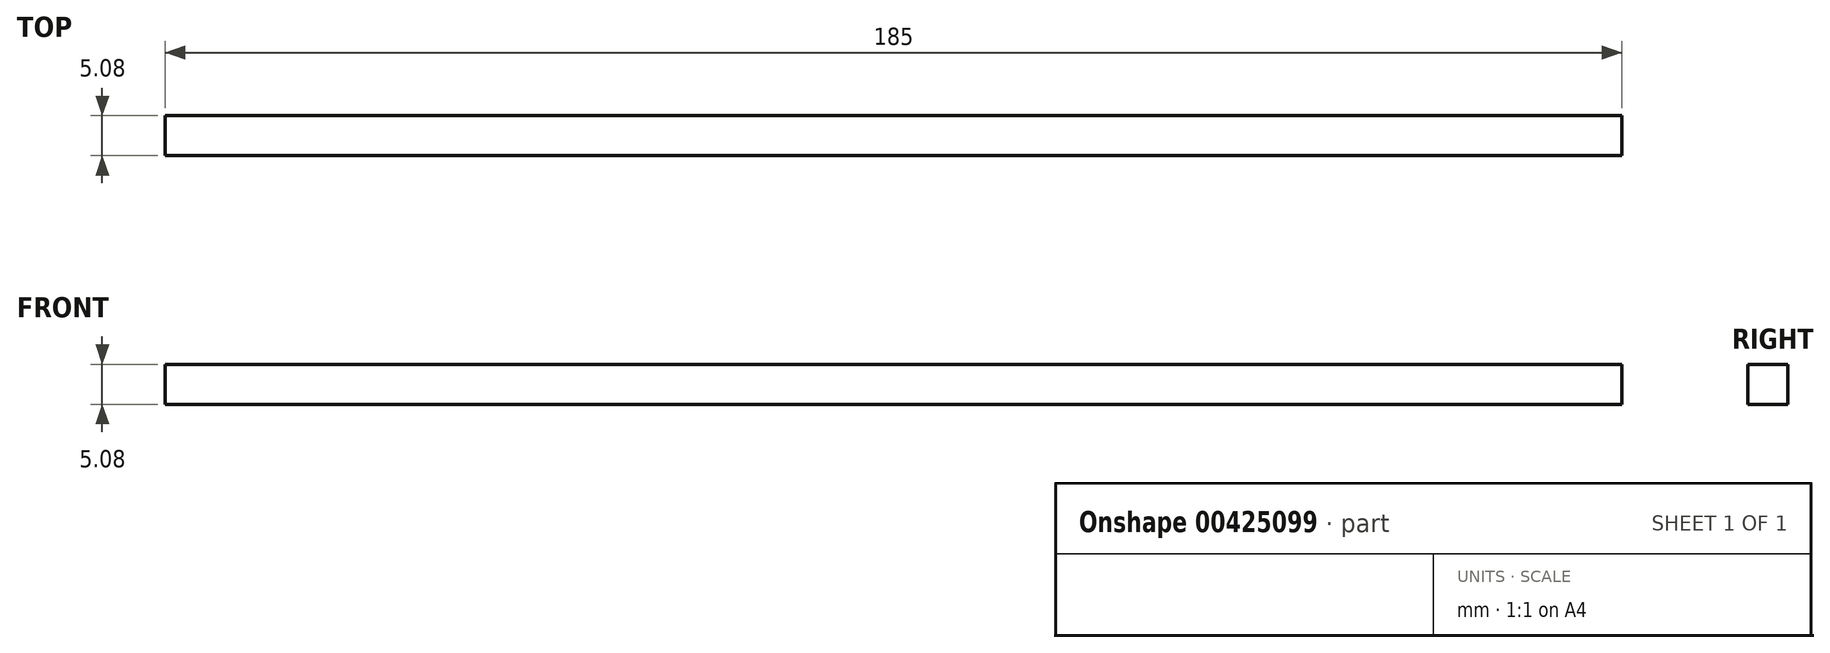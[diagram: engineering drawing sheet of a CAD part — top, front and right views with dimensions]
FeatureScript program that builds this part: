
annotation { "Feature Type Name" : "Feature", "Feature Type Description" : "" }
export const myFeature = defineFeature(function(context is Context, id is Id, definition is map)
    precondition{}
    {
        {
            var Q0;
            Q0=qCreatedBy(makeId("Front.planeOp"),FACE);
            var sketch = newSketch(context, id + "F0", { "sketchPlane" : qUnion([Q0])});
            skLineSegment(sketch, "E0.bottom", {"start": v(-96.89, -50.98) * mm, "end": v(88.11, -50.98) * mm});
            skLineSegment(sketch, "E0.top", {"start": v(-96.89, -56.06) * mm, "end": v(88.11, -56.06) * mm});
            skLineSegment(sketch, "E0.left", {"start": v(-96.89, -50.98) * mm, "end": v(-96.89, -56.06) * mm});
            skLineSegment(sketch, "E0.right", {"start": v(88.11, -50.98) * mm, "end": v(88.11, -56.06) * mm});
            skSolve(sketch);
        }
        {
            var Q0;
            Q0 = qSketchRegion(id + "F0", true);
            extrude(context, id + "F1", {"entities" : qUnion([Q0]), "depth" : 5.08 * mm});
        }
    });
